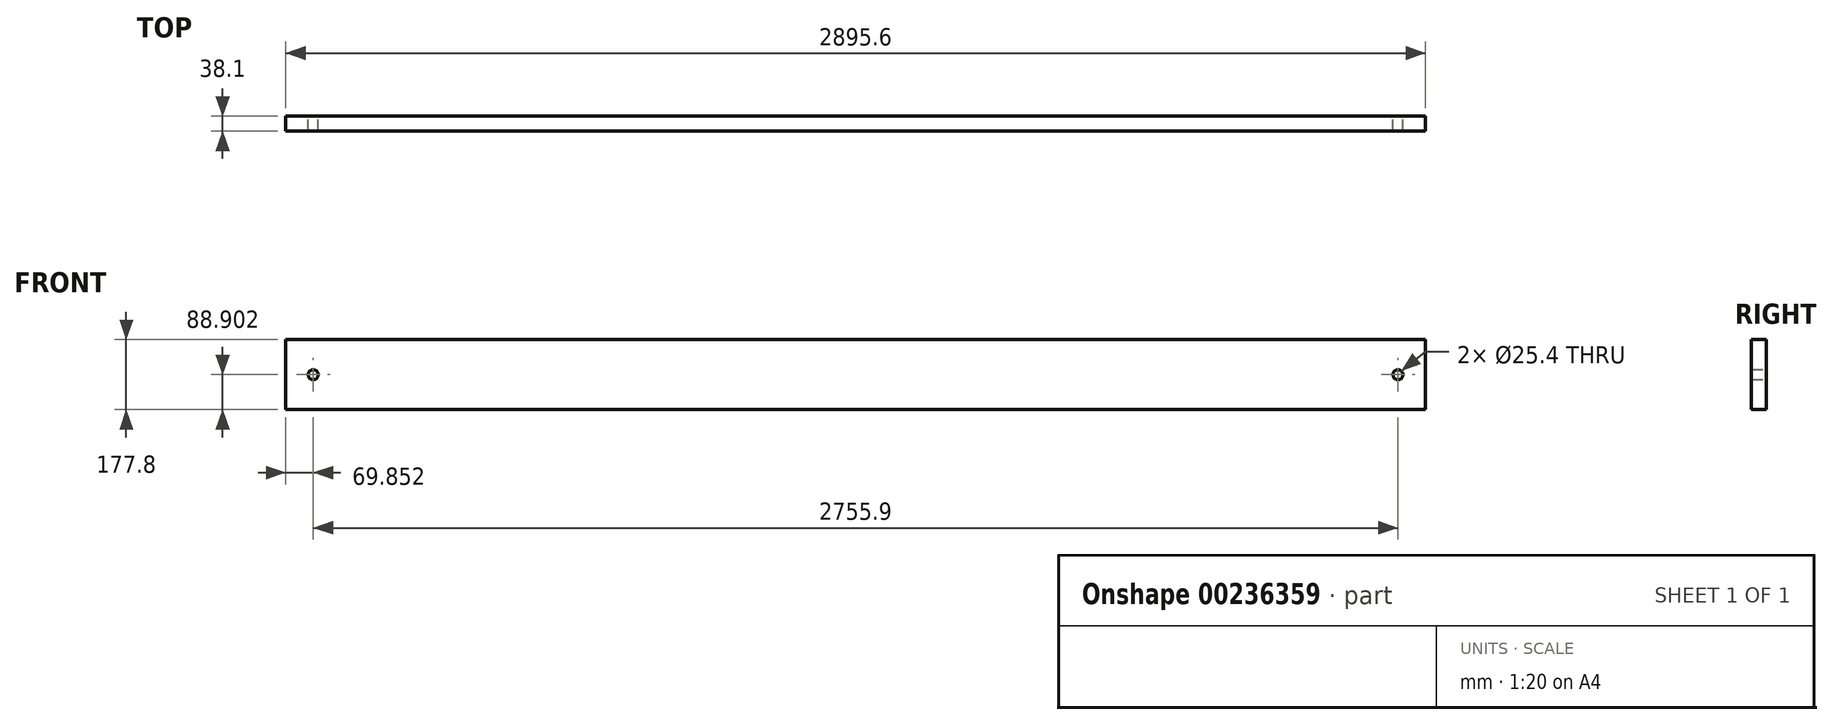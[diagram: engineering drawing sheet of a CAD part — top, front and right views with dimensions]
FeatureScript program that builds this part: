
annotation { "Feature Type Name" : "Feature", "Feature Type Description" : "" }
export const myFeature = defineFeature(function(context is Context, id is Id, definition is map)
    precondition{}
    {
        {
            var Q0;
            Q0=qCreatedBy(makeId("Front.planeOp"),FACE);
            var sketch = newSketch(context, id + "F0", { "sketchPlane" : qUnion([Q0])});
            skLineSegment(sketch, "E0.bottom", {"start": v(-1513.52, -246.22) * mm, "end": v(1382.08, -246.22) * mm});
            skLineSegment(sketch, "E0.top", {"start": v(-1513.52, -424.02) * mm, "end": v(1382.08, -424.02) * mm});
            skLineSegment(sketch, "E0.left", {"start": v(-1513.52, -246.22) * mm, "end": v(-1513.52, -424.02) * mm});
            skLineSegment(sketch, "E0.right", {"start": v(1382.08, -246.22) * mm, "end": v(1382.08, -424.02) * mm});
            skCircle(sketch, "E1", {"center": v(-1443.67, -335.12) * mm, "radius": 12.7 * mm});
            skCircle(sketch, "E2", {"center": v(1312.23, -335.12) * mm, "radius": 12.7 * mm});
            skSolve(sketch);
        }
        {
            var Q0;
            Q0=makeQuery(id+"F0.imprint","IMPRINT",FACE,{"disambiguationData":[TD([[makeQuery(id+"F0.imprint","IMPRINT",EDGE,{"derivedFrom":sQuery(id+"F0.wireOp",EDGE,"E0.bottom")}),-1.0]])]});
            extrude(context, id + "F1", {"entities" : qUnion([Q0]), "depth" : 38.1 * mm});
        }
    });
